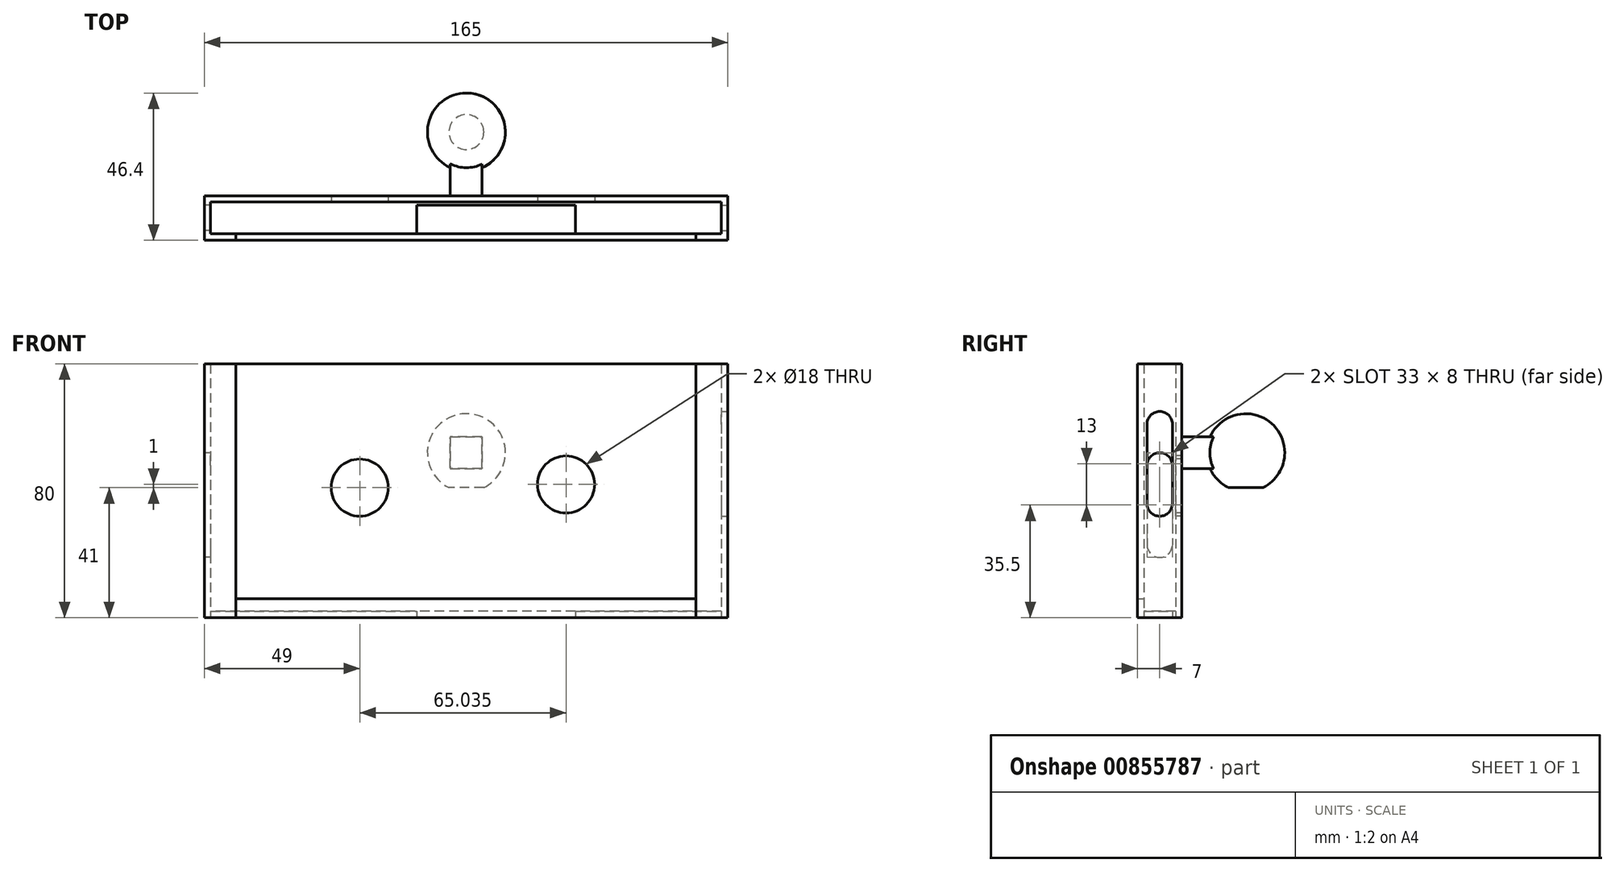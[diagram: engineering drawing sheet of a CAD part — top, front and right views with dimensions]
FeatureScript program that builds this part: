
annotation { "Feature Type Name" : "Feature", "Feature Type Description" : "" }
export const myFeature = defineFeature(function(context is Context, id is Id, definition is map)
    precondition{}
    {
        {
            var Q0;
            Q0=qCreatedBy(makeId("Top.planeOp"),FACE);
            var sketch = newSketch(context, id + "F0", { "sketchPlane" : qUnion([Q0])});
            skLineSegment(sketch, "E0", {"start": v(0, 0) * mm, "end": v(161, 0) * mm});
            skLineSegment(sketch, "E1", {"start": v(161, 0) * mm, "end": v(161, 10) * mm});
            skLineSegment(sketch, "E2", {"start": v(161, 10) * mm, "end": v(0, 10) * mm});
            skLineSegment(sketch, "E3", {"start": v(0, 10) * mm, "end": v(0, 0) * mm});
            skLineSegment(sketch, "E4", {"start": v(0, 10) * mm, "end": v(0, 12) * mm});
            skLineSegment(sketch, "E5", {"start": v(161, 10) * mm, "end": v(161, 12) * mm});
            skLineSegment(sketch, "E6", {"start": v(0, 10) * mm, "end": v(-2, 10) * mm});
            skLineSegment(sketch, "E7", {"start": v(0, 0) * mm, "end": v(-2, 0) * mm});
            skLineSegment(sketch, "E8", {"start": v(0, 0) * mm, "end": v(0, -2) * mm});
            skLineSegment(sketch, "E9", {"start": v(161, 0) * mm, "end": v(161, -2) * mm});
            skLineSegment(sketch, "E10", {"start": v(161, 0) * mm, "end": v(163, 0) * mm});
            skLineSegment(sketch, "E11", {"start": v(161, 10) * mm, "end": v(163, 10) * mm});
            skLineSegment(sketch, "E12", {"start": v(-2, 12) * mm, "end": v(0, 12) * mm});
            skLineSegment(sketch, "E13", {"start": v(-2, 10) * mm, "end": v(-2, 12) * mm});
            skLineSegment(sketch, "E14", {"start": v(-2, 0) * mm, "end": v(-2, -2) * mm});
            skLineSegment(sketch, "E15", {"start": v(-2, -2) * mm, "end": v(0, -2) * mm});
            skLineSegment(sketch, "E16", {"start": v(-2, 0) * mm, "end": v(-2, 10) * mm});
            skLineSegment(sketch, "E17", {"start": v(0, 12) * mm, "end": v(161, 12) * mm});
            skLineSegment(sketch, "E18", {"start": v(163, 12) * mm, "end": v(163, 10) * mm});
            skLineSegment(sketch, "E19", {"start": v(161, 12) * mm, "end": v(163, 12) * mm});
            skLineSegment(sketch, "E20", {"start": v(163, 10) * mm, "end": v(163, 0) * mm});
            skLineSegment(sketch, "E21", {"start": v(163, 0) * mm, "end": v(163, -2) * mm});
            skLineSegment(sketch, "E22", {"start": v(163, -2) * mm, "end": v(161, -2) * mm});
            skLineSegment(sketch, "E23", {"start": v(161, -2) * mm, "end": v(0, -2) * mm});
            skLineSegment(sketch, "E24", {"start": v(0, 0) * mm, "end": v(8, 0) * mm});
            skLineSegment(sketch, "E25", {"start": v(8, 0) * mm, "end": v(8, -2) * mm});
            skLineSegment(sketch, "E26", {"start": v(163, -2) * mm, "end": v(153, -2) * mm});
            skLineSegment(sketch, "E27", {"start": v(153, -2) * mm, "end": v(153, 0) * mm});
            skSolve(sketch);
        }
        {
            var Q0;
            Q0=makeQuery(id+"F0.imprint","IMPRINT",FACE,{"disambiguationData":[TD([[makeQuery(id+"F0.imprint","IMPRINT",EDGE,{"derivedFrom":sQuery(id+"F0.wireOp",EDGE,"E2")}),-1.0]])]});
            var Q1;
            Q1=makeQuery(id+"F0.imprint","IMPRINT",FACE,{"disambiguationData":[TD([[makeQuery(id+"F0.imprint","IMPRINT",EDGE,{"derivedFrom":sQuery(id+"F0.wireOp",EDGE,"E5")}),-1.0]])]});
            var Q2;
            Q2=makeQuery(id+"F0.imprint","IMPRINT",FACE,{"disambiguationData":[TD([[makeQuery(id+"F0.imprint","IMPRINT",EDGE,{"derivedFrom":sQuery(id+"F0.wireOp",EDGE,"E1")}),-1.0]])]});
            var Q3;
            Q3=makeQuery(id+"F0.imprint","IMPRINT",FACE,{"disambiguationData":[TD([[makeQuery(id+"F0.imprint","IMPRINT",EDGE,{"derivedFrom":sQuery(id+"F0.wireOp",EDGE,"E9")}),1.0]])]});
            var Q4;
            {var subQ0=sQuery(id+"F0.wireOp",EDGE,"E9");Q4=makeQuery(id+"F0.imprint","IMPRINT",FACE,{"disambiguationData":[TD([[makeQuery(id+"F0.imprint","IMPRINT",EDGE,{"derivedFrom":subQ0}),-1.0]])]});}
            var Q5;
            Q5=makeQuery(id+"F0.imprint","IMPRINT",FACE,{"disambiguationData":[TD([[makeQuery(id+"F0.imprint","IMPRINT",EDGE,{"derivedFrom":sQuery(id+"F0.wireOp",EDGE,"E4")}),1.0]])]});
            var Q6;
            Q6=makeQuery(id+"F0.imprint","IMPRINT",FACE,{"disambiguationData":[TD([[makeQuery(id+"F0.imprint","IMPRINT",EDGE,{"derivedFrom":sQuery(id+"F0.wireOp",EDGE,"E3")}),-1.0]])]});
            var Q7;
            Q7=makeQuery(id+"F0.imprint","IMPRINT",FACE,{"disambiguationData":[TD([[makeQuery(id+"F0.imprint","IMPRINT",EDGE,{"derivedFrom":sQuery(id+"F0.wireOp",EDGE,"E7")}),1.0]])]});
            var Q8;
            {var subQ2=sQuery(id+"F0.wireOp",EDGE,"E8");Q8=makeQuery(id+"F0.imprint","IMPRINT",FACE,{"disambiguationData":[TD([[makeQuery(id+"F0.imprint","IMPRINT",EDGE,{"derivedFrom":subQ2}),1.0]])]});}
            extrude(context, id + "F1", {"entities" : qUnion([Q0, Q1, Q2, Q3, Q4, Q5, Q6, Q7, Q8]), "depth" : 80 * mm});
        }
        {
            var Q0;
            {var subQ0=sQuery(id+"F0.wireOp",EDGE,"E1");Q0=makeQuery(id+"F0.imprint","IMPRINT",FACE,{"disambiguationData":[TD([[makeQuery(id+"F0.imprint","IMPRINT",EDGE,{"derivedFrom":subQ0}),1.0]])]});}
            extrude(context, id + "F2", {"entities" : qUnion([Q0]), "depth" : 2 * mm});
        }
        {
            var Q0;
            {var subQ0=sQuery(id+"F0.wireOp",EDGE,"E25");Q0=makeQuery(id+"F0.imprint","IMPRINT",FACE,{"disambiguationData":[TD([[makeQuery(id+"F0.imprint","IMPRINT",EDGE,{"derivedFrom":subQ0}),1.0]])]});}
            extrude(context, id + "F3", {"entities" : qUnion([Q0]), "depth" : 6 * mm});
        }
        {
            var Q0;
            Q0=makeQuery(id+"F1.opExtrude","SWEPT_FACE",FACE,{"disambiguationData":[OSD([sQuery(id+"F0.wireOp",EDGE,"E13"),sQuery(id+"F0.wireOp",EDGE,"E14"),sQuery(id+"F0.wireOp",EDGE,"E16")])]});
            var sketch = newSketch(context, id + "F4", { "sketchPlane" : qUnion([Q0])});
            skPoint(sketch, "E28", {"position": v(-4.5, 23) * mm});
            skPoint(sketch, "E29", {"position": v(2, 23) * mm});
            skPoint(sketch, "E30", {"position": v(-5, 0) * mm});
            skPoint(sketch, "E31", {"position": v(-4.5, 48) * mm});
            skLineSegment(sketch, "E32.bottom", {"start": v(-9, 48) * mm, "end": v(-1, 48) * mm});
            skLineSegment(sketch, "E32.top", {"start": v(-9, 23) * mm, "end": v(-1, 23) * mm});
            skLineSegment(sketch, "E32.left", {"start": v(-9, 48) * mm, "end": v(-9, 23) * mm});
            skLineSegment(sketch, "E32.right", {"start": v(-1, 48) * mm, "end": v(-1, 23) * mm});
            skArc(sketch, "E33", {"start": v(-1, 48) * mm, "mid": v(-5, 52) * mm, "end": v(-9, 48) * mm});
            skArc(sketch, "E34", {"start": v(-9, 23) * mm, "mid": v(-5, 19) * mm, "end": v(-1, 23) * mm});
            skSolve(sketch);
        }
        {
            var Q0;
            Q0=makeQuery(id+"F4.imprint","IMPRINT",FACE,{"disambiguationData":[TD([[makeQuery(id+"F4.imprint","IMPRINT",EDGE,{"derivedFrom":sQuery(id+"F4.wireOp",EDGE,"E32.bottom")}),1.0]])]});
            var Q1;
            Q1=makeQuery(id+"F4.imprint","IMPRINT",FACE,{"disambiguationData":[TD([[makeQuery(id+"F4.imprint","IMPRINT",EDGE,{"derivedFrom":sQuery(id+"F4.wireOp",EDGE,"E32.bottom")}),-1.0]])]});
            var Q2;
            Q2=makeQuery(id+"F4.imprint","IMPRINT",FACE,{"disambiguationData":[TD([[makeQuery(id+"F4.imprint","IMPRINT",EDGE,{"derivedFrom":sQuery(id+"F4.wireOp",EDGE,"E32.top")}),-1.0]])]});
            extrude(context, id + "F5", {"entities" : qUnion([Q0, Q1, Q2]), "operationType" : NewBodyOperationType.REMOVE, "endBound" : BoundingType.UP_TO_NEXT, "oppositeDirection" : true, "depth" : 25 * mm});
        }
        {
            var Q0;
            Q0=makeQuery(id+"F1.opExtrude","SWEPT_FACE",FACE,{"disambiguationData":[OSD([sQuery(id+"F0.wireOp",EDGE,"E18"),sQuery(id+"F0.wireOp",EDGE,"E20"),sQuery(id+"F0.wireOp",EDGE,"E21")])]});
            var sketch = newSketch(context, id + "F6", { "sketchPlane" : qUnion([Q0])});
            skPoint(sketch, "E35", {"position": v(5.5, 36) * mm});
            skPoint(sketch, "E36", {"position": v(12, 36) * mm});
            skPoint(sketch, "E37", {"position": v(5, 0) * mm});
            skPoint(sketch, "E38", {"position": v(5.5, 61) * mm});
            skLineSegment(sketch, "E39.bottom", {"start": v(1, 61) * mm, "end": v(9, 61) * mm});
            skLineSegment(sketch, "E39.top", {"start": v(1, 36) * mm, "end": v(9, 36) * mm});
            skLineSegment(sketch, "E39.left", {"start": v(1, 61) * mm, "end": v(1, 36) * mm});
            skLineSegment(sketch, "E39.right", {"start": v(9, 61) * mm, "end": v(9, 36) * mm});
            skArc(sketch, "E40", {"start": v(9, 61) * mm, "mid": v(5, 65) * mm, "end": v(1, 61) * mm});
            skArc(sketch, "E41", {"start": v(1, 36) * mm, "mid": v(5, 32) * mm, "end": v(9, 36) * mm});
            skSolve(sketch);
        }
        {
            var Q0;
            Q0=makeQuery(id+"F6.imprint","IMPRINT",FACE,{"disambiguationData":[TD([[makeQuery(id+"F6.imprint","IMPRINT",EDGE,{"derivedFrom":sQuery(id+"F6.wireOp",EDGE,"E39.bottom")}),1.0]])]});
            var Q1;
            Q1=makeQuery(id+"F6.imprint","IMPRINT",FACE,{"disambiguationData":[TD([[makeQuery(id+"F6.imprint","IMPRINT",EDGE,{"derivedFrom":sQuery(id+"F6.wireOp",EDGE,"E39.bottom")}),-1.0]])]});
            var Q2;
            Q2=makeQuery(id+"F6.imprint","IMPRINT",FACE,{"disambiguationData":[TD([[makeQuery(id+"F6.imprint","IMPRINT",EDGE,{"derivedFrom":sQuery(id+"F6.wireOp",EDGE,"E39.top")}),-1.0]])]});
            extrude(context, id + "F7", {"entities" : qUnion([Q0, Q1, Q2]), "operationType" : NewBodyOperationType.REMOVE, "endBound" : BoundingType.UP_TO_NEXT, "oppositeDirection" : true, "depth" : 25 * mm});
        }
        {
            var Q0;
            Q0=qCreatedBy(makeId("Front.planeOp"),FACE);
            var sketch = newSketch(context, id + "F8", { "sketchPlane" : qUnion([Q0])});
            skPoint(sketch, "E42", {"position": v(47, 0) * mm});
            skPoint(sketch, "E43", {"position": v(47, 41) * mm});
            skCircle(sketch, "E44", {"center": v(47, 41) * mm, "radius": 9 * mm});
            skPoint(sketch, "E45", {"position": v(113, 0) * mm});
            skPoint(sketch, "E46", {"position": v(112.04, 42) * mm});
            skCircle(sketch, "E47", {"center": v(112.04, 42) * mm, "radius": 9 * mm});
            skSolve(sketch);
        }
        {
            var Q0;
            Q0=makeQuery(id+"F8.imprint","IMPRINT",FACE,{"disambiguationData":[TD([[makeQuery(id+"F8.imprint","IMPRINT",EDGE,{"derivedFrom":sQuery(id+"F8.wireOp",EDGE,"E44")}),1.0]])]});
            var Q1;
            Q1=makeQuery(id+"F8.imprint","IMPRINT",FACE,{"disambiguationData":[TD([[makeQuery(id+"F8.imprint","IMPRINT",EDGE,{"derivedFrom":sQuery(id+"F8.wireOp",EDGE,"E47")}),1.0]])]});
            extrude(context, id + "F9", {"entities" : qUnion([Q0, Q1]), "operationType" : NewBodyOperationType.REMOVE, "endBound" : BoundingType.THROUGH_ALL, "oppositeDirection" : true, "depth" : 25 * mm});
        }
        {
            var Q0;
            Q0=makeQuery(id+"F1.opExtrude","SWEPT_FACE",FACE,{"disambiguationData":[OSD([sQuery(id+"F0.wireOp",EDGE,"E12"),sQuery(id+"F0.wireOp",EDGE,"E17"),sQuery(id+"F0.wireOp",EDGE,"E19")])]});
            var sketch = newSketch(context, id + "F10", { "sketchPlane" : qUnion([Q0])});
            skPoint(sketch, "E48", {"position": v(-80.5, 58) * mm});
            skPoint(sketch, "E49.start.orphan", {"position": v(-93, 59) * mm});
            skPoint(sketch, "E50.start.orphan", {"position": v(-93, 58) * mm});
            skPoint(sketch, "E51.start.orphan", {"position": v(-93, 47) * mm});
            skPoint(sketch, "E52.start.orphan", {"position": v(-68, 47) * mm});
            skPoint(sketch, "E53.end.orphan", {"position": v(-68, 58) * mm});
            skLineSegment(sketch, "E54", {"start": v(-75.5, 47) * mm, "end": v(-85.5, 47) * mm});
            skLineSegment(sketch, "E55", {"start": v(-85.5, 47) * mm, "end": v(-85.5, 57) * mm});
            skLineSegment(sketch, "E56", {"start": v(-85.5, 57) * mm, "end": v(-75.5, 57) * mm});
            skLineSegment(sketch, "E57", {"start": v(-75.5, 57) * mm, "end": v(-75.5, 47) * mm});
            skPoint(sketch, "E58.start.orphan", {"position": v(-93, 60) * mm});
            skPoint(sketch, "E59.start.orphan", {"position": v(-95, 60) * mm});
            skPoint(sketch, "E60.end.orphan", {"position": v(-95, 58) * mm});
            skPoint(sketch, "E61.end.orphan", {"position": v(-95, 41) * mm});
            skPoint(sketch, "E61.start.orphan", {"position": v(-93, 41) * mm});
            skPoint(sketch, "E62.start.orphan", {"position": v(-68, 41) * mm});
            skPoint(sketch, "E63.start.orphan", {"position": v(-66, 41) * mm});
            skPoint(sketch, "E64.end.orphan", {"position": v(-68, 60) * mm});
            skPoint(sketch, "E65.end.orphan", {"position": v(-66, 60) * mm});
            skPoint(sketch, "E65.start.orphan", {"position": v(-66, 58) * mm});
            skSolve(sketch);
        }
        {
            var Q0;
            {var subQ0=sQuery(id+"F0.wireOp",EDGE,"E1");Q0=makeQuery(id+"F0.imprint","IMPRINT",FACE,{"disambiguationData":[TD([[makeQuery(id+"F0.imprint","IMPRINT",EDGE,{"derivedFrom":subQ0}),1.0]])]});}
            var sketch = newSketch(context, id + "F11", { "sketchPlane" : qUnion([Q0])});
            skLineSegment(sketch, "E66", {"start": v(0, 0) * mm, "end": v(65, 0) * mm});
            skLineSegment(sketch, "E67", {"start": v(115, 0) * mm, "end": v(65, 0) * mm});
            skLineSegment(sketch, "E68", {"start": v(115, 0) * mm, "end": v(115, 9) * mm});
            skLineSegment(sketch, "E69", {"start": v(115, 9) * mm, "end": v(65, 9) * mm});
            skLineSegment(sketch, "E70", {"start": v(65, 9) * mm, "end": v(65, 0) * mm});
            skSolve(sketch);
        }
        {
            var Q0;
            Q0=makeQuery(id+"F11.imprint","IMPRINT",FACE,{"disambiguationData":[TD([[makeQuery(id+"F11.imprint","IMPRINT",EDGE,{"derivedFrom":sQuery(id+"F11.wireOp",EDGE,"E67")}),1.0]])]});
            extrude(context, id + "F12", {"entities" : qUnion([Q0]), "operationType" : NewBodyOperationType.REMOVE, "endBound" : BoundingType.UP_TO_NEXT, "depth" : 10 * mm, "offsetDistance" : 25 * mm});
        }
        {
            var Q0;
            Q0 = qSketchRegion(id + "F10", true);
            extrude(context, id + "F13", {"entities" : qUnion([Q0]), "operationType" : NewBodyOperationType.ADD, "depth" : 10 * mm, "offsetDistance" : 25 * mm});
        }
        {
            var Q0;
            Q0=makeQuery(id+"F13.opExtrude","CAP_FACE",FACE,{"disambiguationData":[OSD([sQuery(id+"F10.wireOp",EDGE,"E54"),sQuery(id+"F10.wireOp",EDGE,"E55"),sQuery(id+"F10.wireOp",EDGE,"E56"),sQuery(id+"F10.wireOp",EDGE,"E57")])],"isStart":false});
            var sketch = newSketch(context, id + "F14", { "sketchPlane" : qUnion([Q0])});
            skLineSegment(sketch, "E71", {"start": v(-80.5, 57) * mm, "end": v(-80.5, 47) * mm});
            skSolve(sketch);
        }
        {
            var Q0;
            Q0=sQuery(id+"F14.wireOp",EDGE,"E71");
            cPlane(context, id + "F15", {"entities" : qUnion([Q0]), "cplaneType" : CPlaneType.MID_PLANE, "offset" : 25 * mm, "width" : 150 * mm, "height" : 150 * mm});
        }
        {
            var Q0;
            Q0=qCreatedBy(id+"F15.planeOp",FACE);
            var sketch = newSketch(context, id + "F16", { "sketchPlane" : qUnion([Q0])});
            skLineSegment(sketch, "E72", {"start": v(80.62, -19.8) * mm, "end": v(80.62, -44.4) * mm});
            skArc(sketch, "E73", {"start": v(80.62, -19.8) * mm, "mid": v(68.32, -32.1) * mm, "end": v(80.62, -44.4) * mm});
            skSolve(sketch);
        }
        {
            var Q0;
            Q0 = qSketchRegion(id + "F16", true);
            var Q1;
            Q1=sQuery(id+"F16.wireOp",EDGE,"E72");
            revolve(context, id + "F17", {"operationType" : NewBodyOperationType.ADD, "surfaceOperationType" : NewSurfaceOperationType.NEW, "entities" : qUnion([Q0]), "axis" : qUnion([Q1]), "revolveType" : RevolveType.FULL});
        }
        {
            var Q0;
            Q0=qCreatedBy(makeId("Top.planeOp"),FACE);
            var sketch = newSketch(context, id + "F18", { "sketchPlane" : qUnion([Q0])});
            skLineSegment(sketch, "E74.bottom", {"start": v(67.33, 46.01) * mm, "end": v(95.36, 46.01) * mm});
            skLineSegment(sketch, "E74.top", {"start": v(67.33, 19.27) * mm, "end": v(95.36, 19.27) * mm});
            skLineSegment(sketch, "E74.left", {"start": v(67.33, 46.01) * mm, "end": v(67.33, 19.27) * mm});
            skLineSegment(sketch, "E74.right", {"start": v(95.36, 46.01) * mm, "end": v(95.36, 19.27) * mm});
            skSolve(sketch);
        }
        {
            var Q0;
            Q0 = qSketchRegion(id + "F18", true);
            extrude(context, id + "F19", {"entities" : qUnion([Q0]), "operationType" : NewBodyOperationType.REMOVE, "depth" : 41 * mm, "offsetDistance" : 25 * mm});
        }
    });
